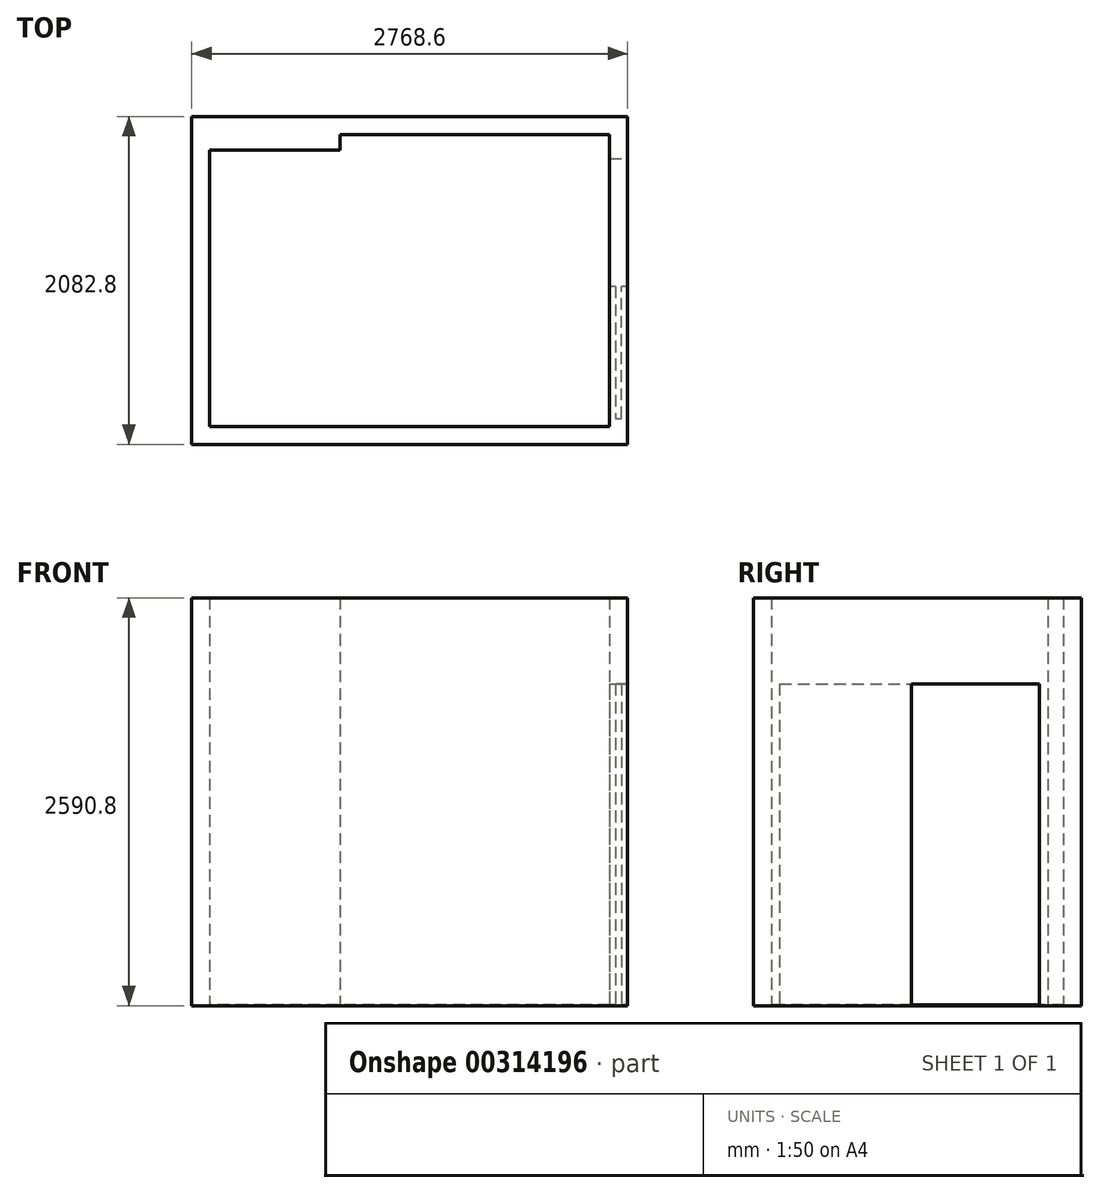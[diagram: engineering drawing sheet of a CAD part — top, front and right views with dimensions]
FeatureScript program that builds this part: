
annotation { "Feature Type Name" : "Feature", "Feature Type Description" : "" }
export const myFeature = defineFeature(function(context is Context, id is Id, definition is map)
    precondition{}
    {
        {
            var Q0;
            Q0=qCreatedBy(makeId("Top.planeOp"),FACE);
            var sketch = newSketch(context, id + "F0", { "sketchPlane" : qUnion([Q0])});
            skLineSegment(sketch, "E0.bottom", {"start": v(0, 0) * mm, "end": v(2768.6, 0) * mm});
            skLineSegment(sketch, "E0.top", {"start": v(0, -2082.8) * mm, "end": v(2768.6, -2082.8) * mm});
            skLineSegment(sketch, "E0.left", {"start": v(0, 0) * mm, "end": v(0, -2082.8) * mm});
            skLineSegment(sketch, "E0.right", {"start": v(2768.6, 0) * mm, "end": v(2768.6, -266.7) * mm});
            skLineSegment(sketch, "E1.bottom", {"start": v(942.98, -114.3) * mm, "end": v(2654.3, -114.3) * mm});
            skLineSegment(sketch, "E1.top", {"start": v(114.3, -1968.5) * mm, "end": v(2654.3, -1968.5) * mm});
            skLineSegment(sketch, "E1.left", {"start": v(114.3, -212.72) * mm, "end": v(114.3, -1968.5) * mm});
            skLineSegment(sketch, "E1.right", {"start": v(2654.3, -114.3) * mm, "end": v(2654.3, -266.7) * mm});
            skLineSegment(sketch, "E2", {"start": v(2654.3, -266.7) * mm, "end": v(2768.6, -266.7) * mm});
            skLineSegment(sketch, "E3", {"start": v(2654.3, -1079.5) * mm, "end": v(2692.4, -1079.5) * mm});
            skLineSegment(sketch, "E4.trimOffspring", {"start": v(2654.3, -1079.5) * mm, "end": v(2654.3, -1968.5) * mm});
            skLineSegment(sketch, "E5.trimOffspring", {"start": v(2768.6, -1079.5) * mm, "end": v(2768.6, -2082.8) * mm});
            skLineSegment(sketch, "E6", {"start": v(2692.4, -1079.5) * mm, "end": v(2692.4, -1917.7) * mm});
            skLineSegment(sketch, "E7", {"start": v(2692.4, -1917.7) * mm, "end": v(2730.5, -1917.7) * mm});
            skLineSegment(sketch, "E8", {"start": v(2730.5, -1917.7) * mm, "end": v(2730.5, -1079.5) * mm});
            skLineSegment(sketch, "E9.trimOffspring", {"start": v(2730.5, -1079.5) * mm, "end": v(2768.6, -1079.5) * mm});
            skLineSegment(sketch, "E10.top", {"start": v(114.3, -212.72) * mm, "end": v(942.98, -212.72) * mm});
            skLineSegment(sketch, "E10.right", {"start": v(942.98, -114.3) * mm, "end": v(942.98, -212.72) * mm});
            skPoint(sketch, "E11.orphan", {"position": v(114.3, -114.3) * mm});
            skSolve(sketch);
        }
        {
            var Q0;
            Q0=makeQuery(id+"F0.imprint","IMPRINT",FACE,{"disambiguationData":[TD([[makeQuery(id+"F0.imprint","IMPRINT",EDGE,{"derivedFrom":sQuery(id+"F0.wireOp",EDGE,"E0.bottom")}),-1.0]])]});
            extrude(context, id + "F1", {"entities" : qUnion([Q0]), "depth" : 2590.8 * mm});
        }
        {
            var Q0;
            Q0=qCreatedBy(makeId("Top.planeOp"),FACE);
            var sketch = newSketch(context, id + "F2", { "sketchPlane" : qUnion([Q0])});
            skLineSegment(sketch, "E12", {"start": v(114.3, -212.73) * mm, "end": v(942.98, -212.73) * mm});
            skLineSegment(sketch, "E13", {"start": v(942.98, -212.73) * mm, "end": v(942.98, -114.3) * mm});
            skLineSegment(sketch, "E14", {"start": v(942.98, -114.3) * mm, "end": v(2654.3, -114.3) * mm});
            skLineSegment(sketch, "E15", {"start": v(2654.3, -114.3) * mm, "end": v(2654.3, -266.7) * mm});
            skLineSegment(sketch, "E16", {"start": v(2654.3, -266.7) * mm, "end": v(2768.6, -266.7) * mm});
            skLineSegment(sketch, "E17", {"start": v(2768.6, -266.7) * mm, "end": v(2768.6, -1079.5) * mm});
            skLineSegment(sketch, "E18", {"start": v(2768.6, -1079.5) * mm, "end": v(2730.5, -1079.5) * mm});
            skLineSegment(sketch, "E19", {"start": v(2654.3, -1079.5) * mm, "end": v(2654.3, -1968.5) * mm});
            skLineSegment(sketch, "E20", {"start": v(2654.3, -1968.5) * mm, "end": v(114.3, -1968.5) * mm});
            skLineSegment(sketch, "E21", {"start": v(114.3, -1968.5) * mm, "end": v(114.3, -212.73) * mm});
            skLineSegment(sketch, "E22", {"start": v(2692.4, -1079.5) * mm, "end": v(2692.4, -1917.7) * mm});
            skLineSegment(sketch, "E23", {"start": v(2692.4, -1917.7) * mm, "end": v(2730.5, -1917.7) * mm});
            skLineSegment(sketch, "E24", {"start": v(2730.5, -1917.7) * mm, "end": v(2730.5, -1079.5) * mm});
            skLineSegment(sketch, "E25.trimOffspring", {"start": v(2692.4, -1079.5) * mm, "end": v(2654.3, -1079.5) * mm});
            skSolve(sketch);
        }
        {
            var Q0;
            Q0=makeQuery(id+"F2.imprint","IMPRINT",FACE,{"disambiguationData":[TD([[makeQuery(id+"F2.imprint","IMPRINT",EDGE,{"derivedFrom":sQuery(id+"F2.wireOp",EDGE,"E12")}),-1.0]])]});
            extrude(context, id + "F3", {"entities" : qUnion([Q0]), "depth" : 6.35 * mm});
        }
        {
            var Q0;
            Q0=qCreatedBy(makeId("Top.planeOp"),FACE);
            cPlane(context, id + "F4", {"entities" : qUnion([Q0]), "cplaneType" : CPlaneType.OFFSET, "offset" : 2044.7 * mm, "width" : 152.4 * mm, "height" : 152.4 * mm});
        }
        {
            var Q0;
            Q0=qCreatedBy(id+"F4.planeOp",FACE);
            var sketch = newSketch(context, id + "F5", { "sketchPlane" : qUnion([Q0])});
            skLineSegment(sketch, "E26", {"start": v(2654.3, -266.7) * mm, "end": v(2654.3, -1079.5) * mm});
            skLineSegment(sketch, "E27", {"start": v(2654.3, -1079.5) * mm, "end": v(2692.4, -1079.5) * mm});
            skLineSegment(sketch, "E28", {"start": v(2692.4, -1079.5) * mm, "end": v(2692.4, -1917.7) * mm});
            skLineSegment(sketch, "E29", {"start": v(2692.4, -1917.7) * mm, "end": v(2730.5, -1917.7) * mm});
            skLineSegment(sketch, "E30", {"start": v(2730.5, -1917.7) * mm, "end": v(2730.5, -1079.5) * mm});
            skLineSegment(sketch, "E31", {"start": v(2730.5, -1079.5) * mm, "end": v(2768.6, -1079.5) * mm});
            skLineSegment(sketch, "E32", {"start": v(2768.6, -1079.5) * mm, "end": v(2768.6, -266.7) * mm});
            skLineSegment(sketch, "E33", {"start": v(2768.6, -266.7) * mm, "end": v(2654.3, -266.7) * mm});
            skSolve(sketch);
        }
        {
            var Q0;
            Q0=makeQuery(id+"F5.imprint","IMPRINT",FACE,{"disambiguationData":[TD([[makeQuery(id+"F5.imprint","IMPRINT",EDGE,{"derivedFrom":sQuery(id+"F5.wireOp",EDGE,"E26")}),1.0]])]});
            extrude(context, id + "F6", {"entities" : qUnion([Q0]), "operationType" : NewBodyOperationType.ADD, "depth" : 546.1 * mm});
        }
    });
